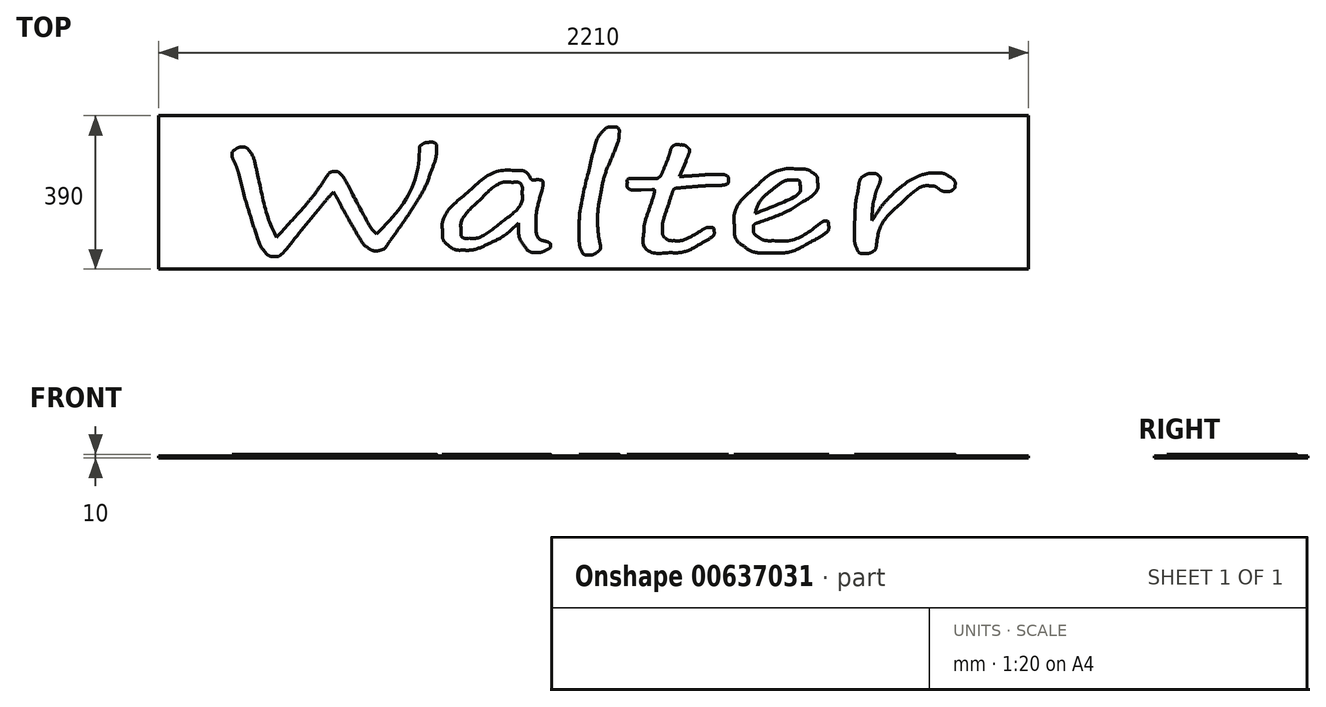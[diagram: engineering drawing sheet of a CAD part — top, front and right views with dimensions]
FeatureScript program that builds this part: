
annotation { "Feature Type Name" : "Feature", "Feature Type Description" : "" }
export const myFeature = defineFeature(function(context is Context, id is Id, definition is map)
    precondition{}
    {
        {
            var Q0;
            Q0=qCreatedBy(makeId("Top.planeOp"),FACE);
            var sketch = newSketch(context, id + "F0", { "sketchPlane" : qUnion([Q0])});
            skFitSpline(sketch, "E0", {"points": [v(-660.5, -1.2) * mm, v(-666.59, -6.81) * mm, v(-677.77, -19.45) * mm, v(-694.06, -39.12) * mm]});
            skFitSpline(sketch, "E1", {"points": [v(-694.06, -39.12) * mm, v(-761.88, -122.43) * mm, v(-799.82, -164.1) * mm, v(-807.88, -164.1) * mm]});
            skFitSpline(sketch, "E2", {"points": [v(-807.88, -164.1) * mm, v(-820.05, -164.1) * mm, v(-829.89, -159.2) * mm, v(-837.4, -149.43) * mm]});
            skFitSpline(sketch, "E3", {"points": [v(-837.4, -149.43) * mm, v(-844.92, -139.78) * mm, v(-855.3, -114.07) * mm, v(-868.54, -72.29) * mm]});
            skFitSpline(sketch, "E4", {"points": [v(-868.54, -72.29) * mm, v(-881.6, -30.5) * mm, v(-892.7, 9.44) * mm, v(-901.83, 47.55) * mm]});
            skFitSpline(sketch, "E5", {"points": [v(-901.83, 47.55) * mm, v(-905.23, 58.3) * mm, v(-908.54, 67.1) * mm, v(-911.76, 73.94) * mm]});
            skFitSpline(sketch, "E6", {"points": [v(-911.76, 73.94) * mm, v(-916.24, 83.1) * mm, v(-918.47, 89.94) * mm, v(-918.47, 94.46) * mm]});
            skFitSpline(sketch, "E7", {"points": [v(-918.47, 94.46) * mm, v(-918.47, 99.22) * mm, v(-915.88, 103.5) * mm, v(-910.69, 107.29) * mm]});
            skFitSpline(sketch, "E8", {"points": [v(-910.69, 107.29) * mm, v(-905.32, 111.2) * mm, v(-899.42, 113.15) * mm, v(-892.97, 113.15) * mm]});
            skFitSpline(sketch, "E9", {"points": [v(-892.97, 113.15) * mm, v(-885.1, 113.15) * mm, v(-878.3, 109) * mm, v(-872.57, 100.7) * mm]});
            skFitSpline(sketch, "E10", {"points": [v(-872.57, 100.7) * mm, v(-866.67, 92.5) * mm, v(-860.13, 72.53) * mm, v(-852.97, 40.77) * mm]});
            skFitSpline(sketch, "E11", {"points": [v(-852.97, 40.77) * mm, v(-837.58, -28.25) * mm, v(-821.84, -80.41) * mm, v(-805.73, -115.72) * mm]});
            skFitSpline(sketch, "E12", {"points": [v(-805.73, -115.72) * mm, v(-760.99, -66.97) * mm, v(-733.16, -36) * mm, v(-722.24, -22.81) * mm]});
            skFitSpline(sketch, "E13", {"points": [v(-722.24, -22.81) * mm, v(-711.33, -9.5) * mm, v(-695.94, 11.94) * mm, v(-676.07, 41.5) * mm]});
            skFitSpline(sketch, "E14", {"points": [v(-676.07, 41.5) * mm, v(-670.88, 47.98) * mm, v(-663.72, 51.22) * mm, v(-654.6, 51.22) * mm]});
            skFitSpline(sketch, "E15", {"points": [v(-654.6, 51.22) * mm, v(-650.66, 51.22) * mm, v(-646.18, 48.53) * mm, v(-641.17, 43.15) * mm]});
            skFitSpline(sketch, "E16", {"points": [v(-641.17, 43.15) * mm, v(-636.16, 37.9) * mm, v(-627.4, 23.3) * mm, v(-614.87, -0.64) * mm]});
            skFitSpline(sketch, "E17", {"points": [v(-614.87, -0.64) * mm, v(-583.73, -59.89) * mm, v(-562.52, -95.44) * mm, v(-551.25, -107.29) * mm]});
            skFitSpline(sketch, "E18", {"points": [v(-551.25, -107.29) * mm, v(-488.25, -36.19) * mm, v(-451.65, 37.53) * mm, v(-441.45, 113.88) * mm]});
            skFitSpline(sketch, "E19", {"points": [v(-441.45, 113.88) * mm, v(-441.45, 115.6) * mm, v(-439.13, 117.91) * mm, v(-434.47, 120.85) * mm]});
            skFitSpline(sketch, "E20", {"points": [v(-434.47, 120.85) * mm, v(-429.64, 123.9) * mm, v(-425.08, 125.43) * mm, v(-420.78, 125.43) * mm]});
            skFitSpline(sketch, "E21", {"points": [v(-420.78, 125.43) * mm, v(-406.47, 125.43) * mm, v(-399.3, 119.2) * mm, v(-399.3, 106.74) * mm]});
            skFitSpline(sketch, "E22", {"points": [v(-399.3, 106.74) * mm, v(-399.3, 93.79) * mm, v(-404.14, 74.36) * mm, v(-413.8, 48.47) * mm]});
            skFitSpline(sketch, "E23", {"points": [v(-413.8, 48.47) * mm, v(-423.29, 22.7) * mm, v(-434.74, -1.13) * mm, v(-448.16, -23) * mm]});
            skFitSpline(sketch, "E24", {"points": [v(-448.16, -23) * mm, v(-461.4, -44.74) * mm, v(-483.78, -77.9) * mm, v(-515.27, -122.5) * mm]});
            skFitSpline(sketch, "E25", {"points": [v(-515.27, -122.5) * mm, v(-520.46, -129.7) * mm, v(-524.85, -136.12) * mm, v(-528.43, -141.74) * mm]});
            skFitSpline(sketch, "E26", {"points": [v(-528.43, -141.74) * mm, v(-530.22, -144.06) * mm, v(-533.7, -146.01) * mm, v(-538.9, -147.6) * mm]});
            skFitSpline(sketch, "E27", {"points": [v(-538.9, -147.6) * mm, v(-543.9, -149.19) * mm, v(-547.93, -149.98) * mm, v(-550.98, -149.98) * mm]});
            skFitSpline(sketch, "E28", {"points": [v(-550.98, -149.98) * mm, v(-558.67, -149.98) * mm, v(-566.46, -147.11) * mm, v(-574.33, -141.37) * mm]});
            skFitSpline(sketch, "E29", {"points": [v(-574.33, -141.37) * mm, v(-582.2, -135.63) * mm, v(-594.2, -118.83) * mm, v(-610.3, -90.98) * mm]});
            skFitSpline(sketch, "E30", {"points": [v(-610.3, -90.98) * mm, v(-626.4, -63) * mm, v(-638.04, -42) * mm, v(-645.2, -27.94) * mm]});
            skFitSpline(sketch, "E31", {"points": [v(-645.2, -27.94) * mm, v(-650.21, -18.3) * mm, v(-655.31, -9.38) * mm, v(-660.5, -1.2) * mm]});
            skFitSpline(sketch, "E32", {"points": [v(-190.73, -79.43) * mm, v(-215.78, -102.4) * mm, v(-240.57, -119.63) * mm, v(-265.09, -131.1) * mm]});
            skFitSpline(sketch, "E33", {"points": [v(-265.09, -131.1) * mm, v(-289.6, -142.6) * mm, v(-312.06, -148.33) * mm, v(-332.47, -148.33) * mm]});
            skFitSpline(sketch, "E34", {"points": [v(-332.47, -148.33) * mm, v(-346.25, -148.33) * mm, v(-358.15, -144.36) * mm, v(-368.17, -136.42) * mm]});
            skFitSpline(sketch, "E35", {"points": [v(-368.17, -136.42) * mm, v(-378.2, -128.48) * mm, v(-383.2, -118.28) * mm, v(-383.2, -105.82) * mm]});
            skFitSpline(sketch, "E36", {"points": [v(-383.2, -105.82) * mm, v(-383.2, -73.7) * mm, v(-362.17, -39.12) * mm, v(-320.12, -2.1) * mm]});
            skFitSpline(sketch, "E37", {"points": [v(-320.12, -2.1) * mm, v(-278.06, 35.03) * mm, v(-236.27, 53.6) * mm, v(-194.75, 53.6) * mm]});
            skFitSpline(sketch, "E38", {"points": [v(-194.75, 53.6) * mm, v(-179.72, 53.6) * mm, v(-168.54, 47.73) * mm, v(-161.2, 36) * mm]});
            skFitSpline(sketch, "E39", {"points": [v(-161.2, 36) * mm, v(-158.87, 32.1) * mm, v(-155.2, 30.14) * mm, v(-150.2, 30.14) * mm]});
            skFitSpline(sketch, "E40", {"points": [v(-150.2, 30.14) * mm, v(-135.88, 30.14) * mm, v(-128.72, 26.36) * mm, v(-128.72, 18.78) * mm]});
            skFitSpline(sketch, "E41", {"points": [v(-128.72, 18.78) * mm, v(-128.72, 15) * mm, v(-129.61, 9.8) * mm, v(-131.4, 3.2) * mm]});
            skFitSpline(sketch, "E42", {"points": [v(-131.4, 3.2) * mm, v(-141.07, -32.83) * mm, v(-145.9, -58.24) * mm, v(-145.9, -73.02) * mm]});
            skFitSpline(sketch, "E43", {"points": [v(-145.9, -73.02) * mm, v(-145.9, -102.58) * mm, v(-137.67, -120.3) * mm, v(-121.2, -126.16) * mm]});
            skFitSpline(sketch, "E44", {"points": [v(-121.2, -126.16) * mm, v(-113.33, -129.1) * mm, v(-109.4, -132.7) * mm, v(-109.4, -136.97) * mm]});
            skFitSpline(sketch, "E45", {"points": [v(-109.4, -136.97) * mm, v(-109.4, -140.76) * mm, v(-113.24, -144.55) * mm, v(-120.93, -148.33) * mm]});
            skFitSpline(sketch, "E46", {"points": [v(-120.93, -148.33) * mm, v(-128.63, -152.24) * mm, v(-136.06, -154.2) * mm, v(-143.21, -154.2) * mm]});
            skFitSpline(sketch, "E47", {"points": [v(-143.21, -154.2) * mm, v(-157, -154.2) * mm, v(-168.36, -147.72) * mm, v(-177.3, -134.77) * mm]});
            skFitSpline(sketch, "E48", {"points": [v(-177.3, -134.77) * mm, v(-186.25, -121.82) * mm, v(-190.73, -103.38) * mm, v(-190.73, -79.43) * mm]});
            skFitSpline(sketch, "E49", {"points": [v(-207.1, 23.73) * mm, v(-230.73, 23.73) * mm, v(-258.2, 8.58) * mm, v(-289.51, -21.71) * mm]});
            skFitSpline(sketch, "E50", {"points": [v(-289.51, -21.71) * mm, v(-320.83, -51.89) * mm, v(-336.5, -76.93) * mm, v(-336.5, -96.84) * mm]});
            skFitSpline(sketch, "E51", {"points": [v(-336.5, -96.84) * mm, v(-336.5, -110.9) * mm, v(-329.7, -117.92) * mm, v(-316.1, -117.92) * mm]});
            skFitSpline(sketch, "E52", {"points": [v(-316.1, -117.92) * mm, v(-296.4, -117.92) * mm, v(-269.11, -104.36) * mm, v(-234.22, -77.24) * mm]});
            skFitSpline(sketch, "E53", {"points": [v(-234.22, -77.24) * mm, v(-199.32, -50.12) * mm, v(-181.87, -25.2) * mm, v(-181.87, -2.47) * mm]});
            skFitSpline(sketch, "E54", {"points": [v(-181.87, -2.47) * mm, v(-181.87, 15) * mm, v(-190.28, 23.73) * mm, v(-207.1, 23.73) * mm]});
            skFitSpline(sketch, "E55", {"points": [v(45.5, 164.1) * mm, v(58.39, 164.1) * mm, v(64.83, 158.47) * mm, v(64.83, 147.23) * mm]});
            skFitSpline(sketch, "E56", {"points": [v(64.83, 147.23) * mm, v(64.83, 137.22) * mm, v(57.04, 113.4) * mm, v(41.47, 75.77) * mm]});
            skFitSpline(sketch, "E57", {"points": [v(41.47, 75.77) * mm, v(31.63, 52.07) * mm, v(24.03, 25.93) * mm, v(18.66, -2.66) * mm]});
            skFitSpline(sketch, "E58", {"points": [v(18.66, -2.66) * mm, v(13.29, -31.24) * mm, v(10.6, -53.66) * mm, v(10.6, -69.9) * mm]});
            skFitSpline(sketch, "E59", {"points": [v(10.6, -69.9) * mm, v(10.6, -90.06) * mm, v(12.48, -110.1) * mm, v(16.24, -130) * mm]});
            skFitSpline(sketch, "E60", {"points": [v(16.24, -130) * mm, v(16.96, -133.8) * mm, v(17.31, -136.54) * mm, v(17.31, -138.25) * mm]});
            skFitSpline(sketch, "E61", {"points": [v(17.31, -138.25) * mm, v(17.31, -144.36) * mm, v(14.27, -149.62) * mm, v(8.19, -154.01) * mm]});
            skFitSpline(sketch, "E62", {"points": [v(8.19, -154.01) * mm, v(2.1, -158.41) * mm, v(-4.34, -160.6) * mm, v(-11.14, -160.6) * mm]});
            skFitSpline(sketch, "E63", {"points": [v(-11.14, -160.6) * mm, v(-20.63, -160.6) * mm, v(-27.25, -156.58) * mm, v(-31, -148.52) * mm]});
            skFitSpline(sketch, "E64", {"points": [v(-31, -148.52) * mm, v(-34.58, -140.45) * mm, v(-36.37, -127.44) * mm, v(-36.37, -109.49) * mm]});
            skFitSpline(sketch, "E65", {"points": [v(-36.37, -109.49) * mm, v(-36.37, -68.56) * mm, v(-29.22, -17.87) * mm, v(-14.9, 42.6) * mm]});
            skFitSpline(sketch, "E66", {"points": [v(-14.9, 42.6) * mm, v(-0.4, 103.07) * mm, v(11.05, 138.44) * mm, v(19.46, 148.7) * mm]});
            skFitSpline(sketch, "E67", {"points": [v(19.46, 148.7) * mm, v(28.05, 158.96) * mm, v(36.73, 164.1) * mm, v(45.5, 164.1) * mm]});
            skFitSpline(sketch, "E68", {"points": [v(218.65, 38.76) * mm, v(237.08, 39.73) * mm, v(254.44, 40.9) * mm, v(270.72, 42.24) * mm]});
            skFitSpline(sketch, "E69", {"points": [v(270.72, 42.24) * mm, v(286.83, 43.46) * mm, v(300.25, 44.07) * mm, v(311, 44.07) * mm]});
            skFitSpline(sketch, "E70", {"points": [v(311, 44.07) * mm, v(324.6, 44.07) * mm, v(333.18, 43.21) * mm, v(336.76, 41.5) * mm]});
            skFitSpline(sketch, "E71", {"points": [v(336.76, 41.5) * mm, v(340.34, 39.8) * mm, v(342.13, 36.8) * mm, v(342.13, 32.53) * mm]});
            skFitSpline(sketch, "E72", {"points": [v(342.13, 32.53) * mm, v(342.13, 22.63) * mm, v(332.02, 17.26) * mm, v(311.8, 16.4) * mm]});
            skFitSpline(sketch, "E73", {"points": [v(311.8, 16.4) * mm, v(285.85, 15.3) * mm, v(261.95, 13.77) * mm, v(240.12, 11.82) * mm]});
            skFitSpline(sketch, "E74", {"points": [v(240.12, 11.82) * mm, v(218.29, 9.86) * mm, v(206.48, 8.22) * mm, v(204.69, 6.87) * mm]});
            skFitSpline(sketch, "E75", {"points": [v(204.69, 6.87) * mm, v(203.08, 5.65) * mm, v(197.7, -8.89) * mm, v(188.58, -36.74) * mm]});
            skFitSpline(sketch, "E76", {"points": [v(188.58, -36.74) * mm, v(179.45, -64.47) * mm, v(174.89, -82.49) * mm, v(174.89, -90.8) * mm]});
            skFitSpline(sketch, "E77", {"points": [v(174.89, -90.8) * mm, v(174.89, -104.23) * mm, v(177.48, -113.21) * mm, v(182.67, -117.73) * mm]});
            skFitSpline(sketch, "E78", {"points": [v(182.67, -117.73) * mm, v(187.86, -122.13) * mm, v(195.65, -124.33) * mm, v(206.03, -124.33) * mm]});
            skFitSpline(sketch, "E79", {"points": [v(206.03, -124.33) * mm, v(221.42, -124.33) * mm, v(242.8, -116.45) * mm, v(270.19, -100.7) * mm]});
            skFitSpline(sketch, "E80", {"points": [v(270.19, -100.7) * mm, v(280.75, -94.22) * mm, v(288.89, -90.98) * mm, v(294.62, -90.98) * mm]});
            skFitSpline(sketch, "E81", {"points": [v(294.62, -90.98) * mm, v(302.31, -90.98) * mm, v(306.16, -93.79) * mm, v(306.16, -99.4) * mm]});
            skFitSpline(sketch, "E82", {"points": [v(306.16, -99.4) * mm, v(306.16, -108.2) * mm, v(293.72, -119.63) * mm, v(268.84, -133.67) * mm]});
            skFitSpline(sketch, "E83", {"points": [v(268.84, -133.67) * mm, v(244.15, -147.6) * mm, v(218.83, -154.56) * mm, v(192.88, -154.56) * mm]});
            skFitSpline(sketch, "E84", {"points": [v(192.88, -154.56) * mm, v(149.57, -154.56) * mm, v(127.91, -137.16) * mm, v(127.91, -102.34) * mm]});
            skFitSpline(sketch, "E85", {"points": [v(127.91, -102.34) * mm, v(127.91, -89.76) * mm, v(132.39, -70.27) * mm, v(141.33, -43.89) * mm]});
            skFitSpline(sketch, "E86", {"points": [v(141.33, -43.89) * mm, v(150.1, -17.62) * mm, v(154.49, -1.86) * mm, v(154.49, 3.39) * mm]});
            skFitSpline(sketch, "E87", {"points": [v(154.49, 3.39) * mm, v(154.49, 5.22) * mm, v(152.34, 6.14) * mm, v(148.05, 6.14) * mm]});
            skFitSpline(sketch, "E88", {"points": [v(120.13, 4.49) * mm, v(97.22, 4.49) * mm, v(85.77, 10.72) * mm, v(85.77, 23.18) * mm]});
            skFitSpline(sketch, "E89", {"points": [v(85.77, 23.18) * mm, v(85.77, 30.27) * mm, v(91.05, 33.8) * mm, v(101.6, 33.8) * mm]});
            skLineSegment(sketch, "E90", {"start": v(148.05, 6.14) * mm, "end": v(120.13, 4.49) * mm});
            skLineSegment(sketch, "E91", {"start": v(120.13, 4.49) * mm, "end": v(148.05, 6.14) * mm});
            skFitSpline(sketch, "E92", {"points": [v(156.9, 33.8) * mm, v(160.66, 33.8) * mm, v(163.97, 34.97) * mm, v(166.84, 37.29) * mm]});
            skFitSpline(sketch, "E93", {"points": [v(166.84, 37.29) * mm, v(169.7, 39.61) * mm, v(173.9, 47.37) * mm, v(179.45, 60.56) * mm]});
            skFitSpline(sketch, "E94", {"points": [v(179.45, 60.56) * mm, v(185, 73.88) * mm, v(189.92, 87) * mm, v(194.22, 99.96) * mm]});
            skFitSpline(sketch, "E95", {"points": [v(194.22, 99.96) * mm, v(198.51, 112.78) * mm, v(206.92, 119.2) * mm, v(219.45, 119.2) * mm]});
            skFitSpline(sketch, "E96", {"points": [v(219.45, 119.2) * mm, v(227.15, 119.2) * mm, v(233.14, 117.37) * mm, v(237.44, 113.7) * mm]});
            skFitSpline(sketch, "E97", {"points": [v(237.44, 113.7) * mm, v(241.73, 110.04) * mm, v(243.88, 106.62) * mm, v(243.88, 103.44) * mm]});
            skFitSpline(sketch, "E98", {"points": [v(243.88, 103.44) * mm, v(243.88, 101.73) * mm, v(240.66, 93) * mm, v(234.22, 77.24) * mm]});
            skLineSegment(sketch, "E99", {"start": v(101.6, 33.8) * mm, "end": v(156.9, 33.8) * mm});
            skLineSegment(sketch, "E100", {"start": v(156.9, 33.8) * mm, "end": v(101.6, 33.8) * mm});
            skFitSpline(sketch, "E101", {"points": [v(596.88, -84.02) * mm, v(596.88, -96.48) * mm, v(580.68, -111.5) * mm, v(548.3, -129.1) * mm]});
            skFitSpline(sketch, "E102", {"points": [v(548.3, -129.1) * mm, v(516.08, -146.68) * mm, v(482.8, -155.48) * mm, v(448.43, -155.48) * mm]});
            skFitSpline(sketch, "E103", {"points": [v(448.43, -155.48) * mm, v(419.62, -155.48) * mm, v(397.34, -149.68) * mm, v(381.6, -138.07) * mm]});
            skFitSpline(sketch, "E104", {"points": [v(381.6, -138.07) * mm, v(366.02, -126.47) * mm, v(358.24, -110.28) * mm, v(358.24, -89.51) * mm]});
            skFitSpline(sketch, "E105", {"points": [v(358.24, -89.51) * mm, v(358.24, -54.58) * mm, v(375.5, -21.35) * mm, v(410.05, 10.17) * mm]});
            skFitSpline(sketch, "E106", {"points": [v(410.05, 10.17) * mm, v(444.58, 41.69) * mm, v(482.35, 57.45) * mm, v(523.33, 57.45) * mm]});
            skFitSpline(sketch, "E107", {"points": [v(523.33, 57.45) * mm, v(536.75, 57.45) * mm, v(547.67, 54.45) * mm, v(556.08, 48.47) * mm]});
            skFitSpline(sketch, "E108", {"points": [v(556.08, 48.47) * mm, v(564.67, 42.48) * mm, v(568.96, 35.27) * mm, v(568.96, 26.84) * mm]});
            skFitSpline(sketch, "E109", {"points": [v(568.96, 26.84) * mm, v(568.96, 8.03) * mm, v(555.45, -9.99) * mm, v(528.43, -27.21) * mm]});
            skFitSpline(sketch, "E110", {"points": [v(528.43, -27.21) * mm, v(501.4, -44.44) * mm, v(465.25, -61.35) * mm, v(419.98, -77.97) * mm]});
            skFitSpline(sketch, "E111", {"points": [v(419.98, -77.97) * mm, v(410.67, -81.27) * mm, v(406.02, -85.54) * mm, v(406.02, -90.8) * mm]});
            skFitSpline(sketch, "E112", {"points": [v(406.02, -90.8) * mm, v(406.02, -100.93) * mm, v(410.31, -109.06) * mm, v(418.9, -115.17) * mm]});
            skFitSpline(sketch, "E113", {"points": [v(418.9, -115.17) * mm, v(427.5, -121.27) * mm, v(440.2, -124.33) * mm, v(457.02, -124.33) * mm]});
            skFitSpline(sketch, "E114", {"points": [v(457.02, -124.33) * mm, v(495.5, -124.33) * mm, v(534.78, -109.8) * mm, v(574.87, -80.72) * mm]});
            skFitSpline(sketch, "E115", {"points": [v(574.87, -80.72) * mm, v(580.77, -76.69) * mm, v(585.25, -74.67) * mm, v(588.3, -74.67) * mm]});
            skFitSpline(sketch, "E116", {"points": [v(588.3, -74.67) * mm, v(594.02, -74.67) * mm, v(596.88, -77.79) * mm, v(596.88, -84.02) * mm]});
            skLineSegment(sketch, "E117", {"start": v(234.22, 77.24) * mm, "end": v(218.65, 38.76) * mm});
            skLineSegment(sketch, "E118", {"start": v(218.65, 38.76) * mm, "end": v(234.22, 77.24) * mm});
            skFitSpline(sketch, "E119", {"points": [v(410.31, -55.43) * mm, v(486.2, -24.65) * mm, v(524.13, 0.1) * mm, v(524.13, 18.78) * mm]});
            skFitSpline(sketch, "E120", {"points": [v(524.13, 18.78) * mm, v(524.13, 26.11) * mm, v(519.3, 29.78) * mm, v(509.64, 29.78) * mm]});
            skFitSpline(sketch, "E121", {"points": [v(509.64, 29.78) * mm, v(493.17, 29.78) * mm, v(474.56, 21.53) * mm, v(453.8, 5.04) * mm]});
            skFitSpline(sketch, "E122", {"points": [v(453.8, 5.04) * mm, v(433.22, -11.45) * mm, v(418.72, -31.6) * mm, v(410.31, -55.43) * mm]});
            skFitSpline(sketch, "E123", {"points": [v(706.94, -73.39) * mm, v(708.73, -71.19) * mm, v(710.88, -68.13) * mm, v(713.38, -64.23) * mm]});
            skFitSpline(sketch, "E124", {"points": [v(713.38, -64.23) * mm, v(725.55, -45.17) * mm, v(736.74, -30.27) * mm, v(746.94, -19.52) * mm]});
            skFitSpline(sketch, "E125", {"points": [v(746.94, -19.52) * mm, v(757.14, -8.64) * mm, v(768.33, 1.74) * mm, v(780.5, 11.64) * mm]});
            skFitSpline(sketch, "E126", {"points": [v(780.5, 11.64) * mm, v(792.84, 21.53) * mm, v(804.03, 29.04) * mm, v(814.05, 34.17) * mm]});
            skFitSpline(sketch, "E127", {"points": [v(814.05, 34.17) * mm, v(824.25, 39.3) * mm, v(833.47, 42.85) * mm, v(841.7, 44.8) * mm]});
            skFitSpline(sketch, "E128", {"points": [v(841.7, 44.8) * mm, v(849.93, 46.88) * mm, v(857.9, 47.92) * mm, v(865.6, 47.92) * mm]});
            skFitSpline(sketch, "E129", {"points": [v(865.6, 47.92) * mm, v(881.16, 47.92) * mm, v(893.87, 44.68) * mm, v(903.71, 38.2) * mm]});
            skFitSpline(sketch, "E130", {"points": [v(903.71, 38.2) * mm, v(913.55, 31.85) * mm, v(918.47, 24.4) * mm, v(918.47, 15.85) * mm]});
            skFitSpline(sketch, "E131", {"points": [v(918.47, 15.85) * mm, v(918.47, 12.06) * mm, v(916.68, 8.64) * mm, v(913.1, 5.59) * mm]});
            skFitSpline(sketch, "E132", {"points": [v(913.1, 5.59) * mm, v(909.7, 2.53) * mm, v(904.43, 1) * mm, v(897.27, 1) * mm]});
            skFitSpline(sketch, "E133", {"points": [v(897.27, 1) * mm, v(889.75, 1) * mm, v(882.86, 3.27) * mm, v(876.6, 7.79) * mm]});
            skFitSpline(sketch, "E134", {"points": [v(876.6, 7.79) * mm, v(870.15, 12.3) * mm, v(863.44, 14.57) * mm, v(856.46, 14.57) * mm]});
            skFitSpline(sketch, "E135", {"points": [v(856.46, 14.57) * mm, v(837.85, 14.57) * mm, v(812.08, -0.82) * mm, v(779.15, -31.6) * mm]});
            skFitSpline(sketch, "E136", {"points": [v(779.15, -31.6) * mm, v(746.22, -62.4) * mm, v(726.18, -96.3) * mm, v(719.02, -133.3) * mm]});
            skFitSpline(sketch, "E137", {"points": [v(719.02, -133.3) * mm, v(717.23, -142.84) * mm, v(713.83, -149.13) * mm, v(708.82, -152.18) * mm]});
            skFitSpline(sketch, "E138", {"points": [v(708.82, -152.18) * mm, v(703.81, -155.23) * mm, v(696.74, -156.76) * mm, v(687.61, -156.76) * mm]});
            skFitSpline(sketch, "E139", {"points": [v(687.61, -156.76) * mm, v(678.85, -156.76) * mm, v(672.5, -152.3) * mm, v(668.55, -143.39) * mm]});
            skFitSpline(sketch, "E140", {"points": [v(668.55, -143.39) * mm, v(664.62, -134.47) * mm, v(662.65, -119.44) * mm, v(662.65, -98.3) * mm]});
            skFitSpline(sketch, "E141", {"points": [v(662.65, -98.3) * mm, v(662.65, -92.57) * mm, v(663.1, -79.92) * mm, v(664, -60.38) * mm]});
            skFitSpline(sketch, "E142", {"points": [v(664, -60.38) * mm, v(665.07, -37.29) * mm, v(667.21, -18.66) * mm, v(670.43, -4.49) * mm]});
            skFitSpline(sketch, "E143", {"points": [v(670.43, -4.49) * mm, v(670.97, -2.17) * mm, v(671.87, 3.27) * mm, v(673.12, 11.82) * mm]});
            skFitSpline(sketch, "E144", {"points": [v(673.12, 11.82) * mm, v(674.37, 21.23) * mm, v(675.9, 27.76) * mm, v(677.68, 31.43) * mm]});
            skFitSpline(sketch, "E145", {"points": [v(677.68, 31.43) * mm, v(679.65, 35.1) * mm, v(683.5, 38.51) * mm, v(689.22, 41.69) * mm]});
            skFitSpline(sketch, "E146", {"points": [v(689.22, 41.69) * mm, v(695.13, 44.86) * mm, v(701.48, 46.45) * mm, v(708.28, 46.45) * mm]});
            skFitSpline(sketch, "E147", {"points": [v(708.28, 46.45) * mm, v(714.9, 46.45) * mm, v(719.83, 44.99) * mm, v(723.05, 42.05) * mm]});
            skFitSpline(sketch, "E148", {"points": [v(723.05, 42.05) * mm, v(726.45, 39.24) * mm, v(728.15, 36.19) * mm, v(728.15, 32.9) * mm]});
            skFitSpline(sketch, "E149", {"points": [v(728.15, 32.9) * mm, v(728.15, 28.13) * mm, v(726.36, 21.4) * mm, v(722.78, 12.73) * mm]});
            skFitSpline(sketch, "E150", {"points": [v(722.78, 12.73) * mm, v(718.66, 3.08) * mm, v(716.25, -3.57) * mm, v(715.53, -7.24) * mm]});
            skFitSpline(sketch, "E151", {"points": [v(715.53, -7.24) * mm, v(715, -11.4) * mm, v(714.01, -15.73) * mm, v(712.58, -20.25) * mm]});
            skFitSpline(sketch, "E152", {"points": [v(712.58, -20.25) * mm, v(710.79, -25.5) * mm, v(709, -39.3) * mm, v(707.21, -61.66) * mm]});
            skLineSegment(sketch, "E153", {"start": v(707.21, -61.66) * mm, "end": v(706.94, -68.44) * mm});
            skLineSegment(sketch, "E154", {"start": v(706.94, -68.44) * mm, "end": v(706.94, -73.39) * mm});
            skLineSegment(sketch, "E155", {"start": v(706.94, -73.39) * mm, "end": v(706.94, -73.39) * mm});
            skLineSegment(sketch, "E156", {"start": v(706.94, -73.39) * mm, "end": v(707.21, -61.66) * mm});
            skSolve(sketch);
        }
        {
            var Q0;
            Q0=qCreatedBy(makeId("Top.planeOp"),FACE);
            var sketch = newSketch(context, id + "F1", { "sketchPlane" : qUnion([Q0])});
            skLineSegment(sketch, "E157.bottom", {"start": v(-1105.32, 193.14) * mm, "end": v(1104.68, 193.14) * mm});
            skLineSegment(sketch, "E157.top", {"start": v(-1105.32, -196.86) * mm, "end": v(1104.68, -196.86) * mm});
            skLineSegment(sketch, "E157.left", {"start": v(-1105.32, 193.14) * mm, "end": v(-1105.32, -196.86) * mm});
            skLineSegment(sketch, "E157.right", {"start": v(1104.68, 193.14) * mm, "end": v(1104.68, -196.86) * mm});
            skSolve(sketch);
        }
        {
            var Q0;
            Q0 = qSketchRegion(id + "F0", true);
            extrude(context, id + "F2", {"entities" : qUnion([Q0]), "depth" : 10 * mm, "offsetDistance" : 25 * mm});
        }
        {
            var Q0;
            Q0 = qSketchRegion(id + "F1", true);
            extrude(context, id + "F3", {"entities" : qUnion([Q0]), "operationType" : NewBodyOperationType.ADD, "depth" : 5 * mm, "offsetDistance" : 25 * mm});
        }
    });
